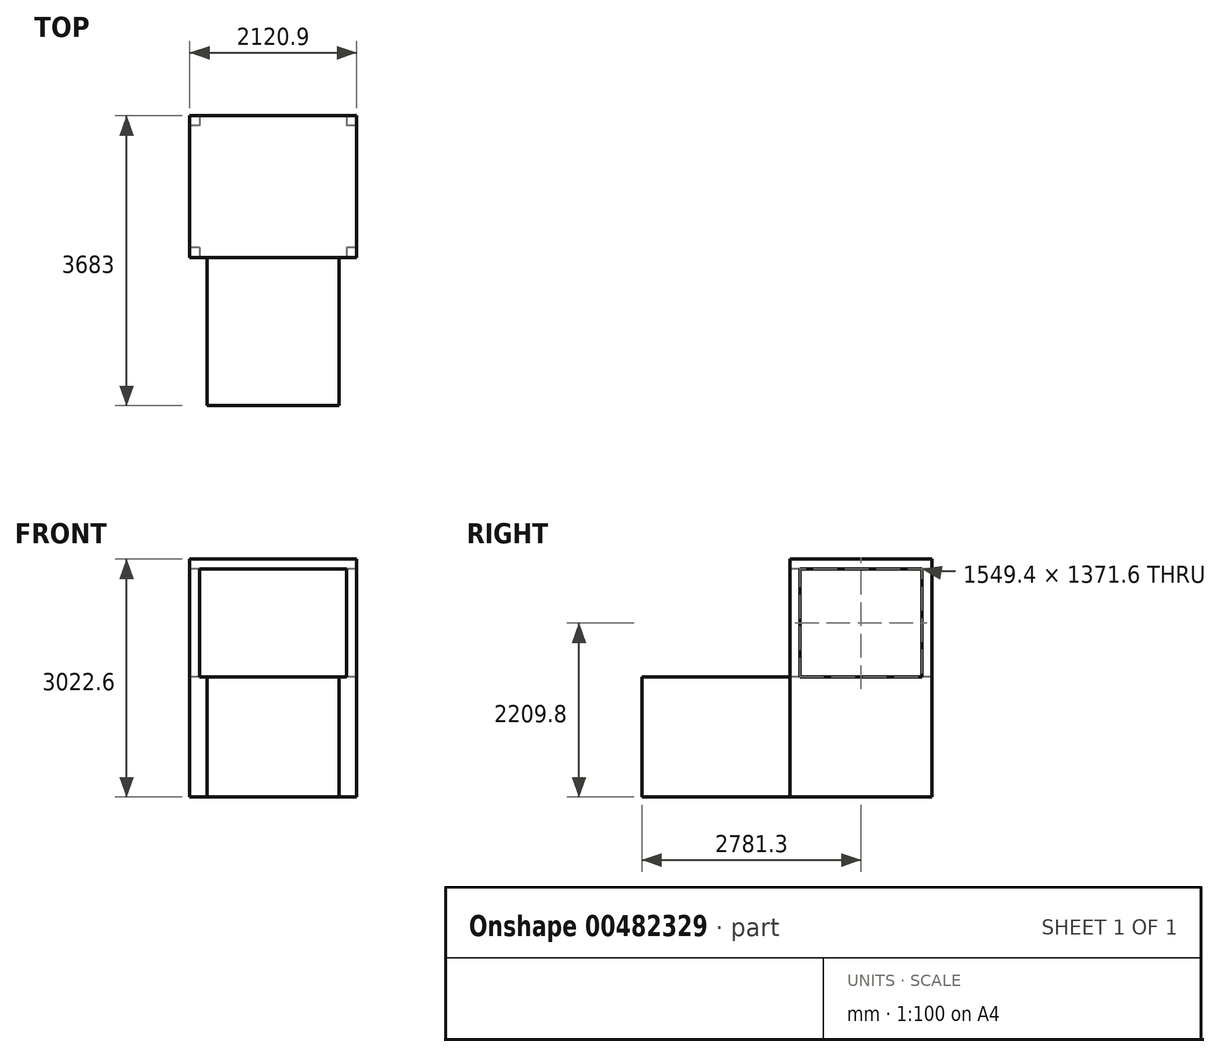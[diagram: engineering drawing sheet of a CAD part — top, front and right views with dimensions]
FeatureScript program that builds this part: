
annotation { "Feature Type Name" : "Feature", "Feature Type Description" : "" }
export const myFeature = defineFeature(function(context is Context, id is Id, definition is map)
    precondition{}
    {
        {
            var Q0;
            Q0=qCreatedBy(makeId("Top.planeOp"),FACE);
            var sketch = newSketch(context, id + "F0", { "sketchPlane" : qUnion([Q0])});
            skLineSegment(sketch, "E0.bottom", {"start": v(0, 0) * mm, "end": v(2120.9, 0) * mm});
            skLineSegment(sketch, "E0.top", {"start": v(0, 1803.4) * mm, "end": v(2120.9, 1803.4) * mm});
            skLineSegment(sketch, "E0.left", {"start": v(0, 0) * mm, "end": v(0, 1803.4) * mm});
            skLineSegment(sketch, "E0.right", {"start": v(2120.9, 0) * mm, "end": v(2120.9, 1803.4) * mm});
            skSolve(sketch);
        }
        {
            var Q0;
            Q0 = qSketchRegion(id + "F0", true);
            extrude(context, id + "F1", {"entities" : qUnion([Q0]), "depth" : 3022.6 * mm, "offsetDistance" : 25.4 * mm});
        }
        {
            var Q0;
            Q0=qCreatedBy(makeId("Top.planeOp"),FACE);
            var sketch = newSketch(context, id + "F2", { "sketchPlane" : qUnion([Q0])});
            skLineSegment(sketch, "E1.bottom", {"start": v(222.25, 0) * mm, "end": v(1898.65, 0) * mm});
            skLineSegment(sketch, "E1.top", {"start": v(222.25, -1879.6) * mm, "end": v(1898.65, -1879.6) * mm});
            skLineSegment(sketch, "E1.left", {"start": v(222.25, 0) * mm, "end": v(222.25, -1879.6) * mm});
            skLineSegment(sketch, "E1.right", {"start": v(1898.65, 0) * mm, "end": v(1898.65, -1879.6) * mm});
            skPoint(sketch, "E2", {"position": v(1060.45, 0) * mm});
            skSolve(sketch);
        }
        {
            var Q0;
            Q0 = qSketchRegion(id + "F2", true);
            extrude(context, id + "F3", {"entities" : qUnion([Q0]), "operationType" : NewBodyOperationType.ADD, "depth" : 1524 * mm, "offsetDistance" : 25.4 * mm});
        }
        {
            var Q0;
            Q0=makeQuery(id+"F1.opExtrude","SWEPT_FACE",FACE,{"disambiguationData":[OSD([sQuery(id+"F0.wireOp",EDGE,"E0.bottom")])]});
            var sketch = newSketch(context, id + "F4", { "sketchPlane" : qUnion([Q0])});
            skLineSegment(sketch, "E3.bottom", {"start": v(127, 2895.6) * mm, "end": v(1993.9, 2895.6) * mm});
            skLineSegment(sketch, "E3.top", {"start": v(127, 1524) * mm, "end": v(1993.9, 1524) * mm});
            skLineSegment(sketch, "E3.left", {"start": v(127, 2895.6) * mm, "end": v(127, 1524) * mm});
            skLineSegment(sketch, "E3.right", {"start": v(1993.9, 2895.6) * mm, "end": v(1993.9, 1524) * mm});
            skSolve(sketch);
        }
        {
            var Q0;
            Q0 = qSketchRegion(id + "F4", true);
            extrude(context, id + "F5", {"entities" : qUnion([Q0]), "operationType" : NewBodyOperationType.REMOVE, "endBound" : BoundingType.THROUGH_ALL, "oppositeDirection" : true, "depth" : 25.4 * mm, "offsetDistance" : 25.4 * mm});
        }
        {
            var Q0;
            Q0=makeQuery(id+"F1.opExtrude","SWEPT_FACE",FACE,{"disambiguationData":[OSD([sQuery(id+"F0.wireOp",EDGE,"E0.left")])]});
            var sketch = newSketch(context, id + "F6", { "sketchPlane" : qUnion([Q0])});
            skLineSegment(sketch, "E4.bottom", {"start": v(-1676.4, 2895.6) * mm, "end": v(-127, 2895.6) * mm});
            skLineSegment(sketch, "E4.top", {"start": v(-1676.4, 1524) * mm, "end": v(-127, 1524) * mm});
            skLineSegment(sketch, "E4.left", {"start": v(-1676.4, 2895.6) * mm, "end": v(-1676.4, 1524) * mm});
            skLineSegment(sketch, "E4.right", {"start": v(-127, 2895.6) * mm, "end": v(-127, 1524) * mm});
            skSolve(sketch);
        }
        {
            var Q0;
            Q0 = qSketchRegion(id + "F6", true);
            extrude(context, id + "F7", {"entities" : qUnion([Q0]), "operationType" : NewBodyOperationType.REMOVE, "endBound" : BoundingType.THROUGH_ALL, "oppositeDirection" : true, "depth" : 25.4 * mm, "offsetDistance" : 25.4 * mm});
        }
    });
